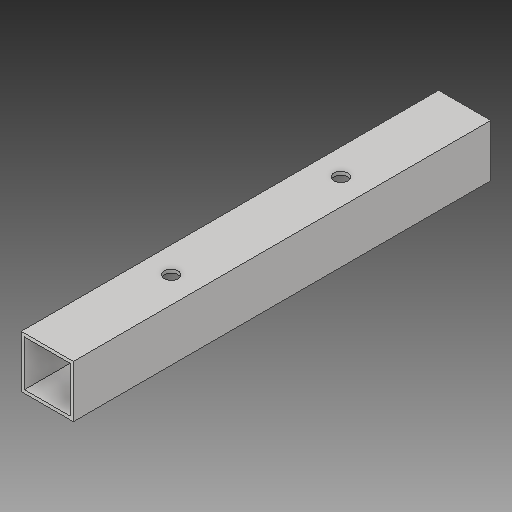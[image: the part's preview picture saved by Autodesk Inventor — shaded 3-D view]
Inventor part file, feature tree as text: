
AUTODESK INVENTOR PART (.ipt)
format: ipt  version: 2019.3 (Build 233278000, 278)  size: 104,448 bytes
history: native  units: in
note: dims shown in document units (in); Inventor stores cm internally (conversion verified against a paired STEP export)
features: hole x4, sketch x3, extrude x1
ambient origin geometry x8: Origin, YZ Plane, XZ Plane, XY Plane, X Axis, Y Axis, Z Axis, Center Point
bodies: Solid1 (feature_tree)
feature tree (8):
  extrude  "Extrusion1"  Depth=1.0in
  hole  "Hole5"  [1 undecoded]
  hole  "Hole7"  [1 undecoded]
  sketch  "Sketch1"  dims[d0=1.0in d1=1.0in]
  sketch  "Sketch4"  dims[d2=0.875in d3=8.0in d4=0.0in]
  hole  "Hole4"  [1 undecoded]
  sketch  "Sketch5"  dims[d19=0.266in d20=0.75in d21=0.375in d22=0.25in d23=0.5635in d24=1.0in d25=0.0in d26=0.266in d27=0.75in d28=0.375in d29=0.25in d30=0.5635in d31=1.0in d32=0.0in]
  hole  "Hole6"  [1 undecoded]
note: 4 required parameter values undecoded (feature->parameter linkage not recoverable at this tier; creation-order binding heuristic only, values carry confidence <= 0.55)
